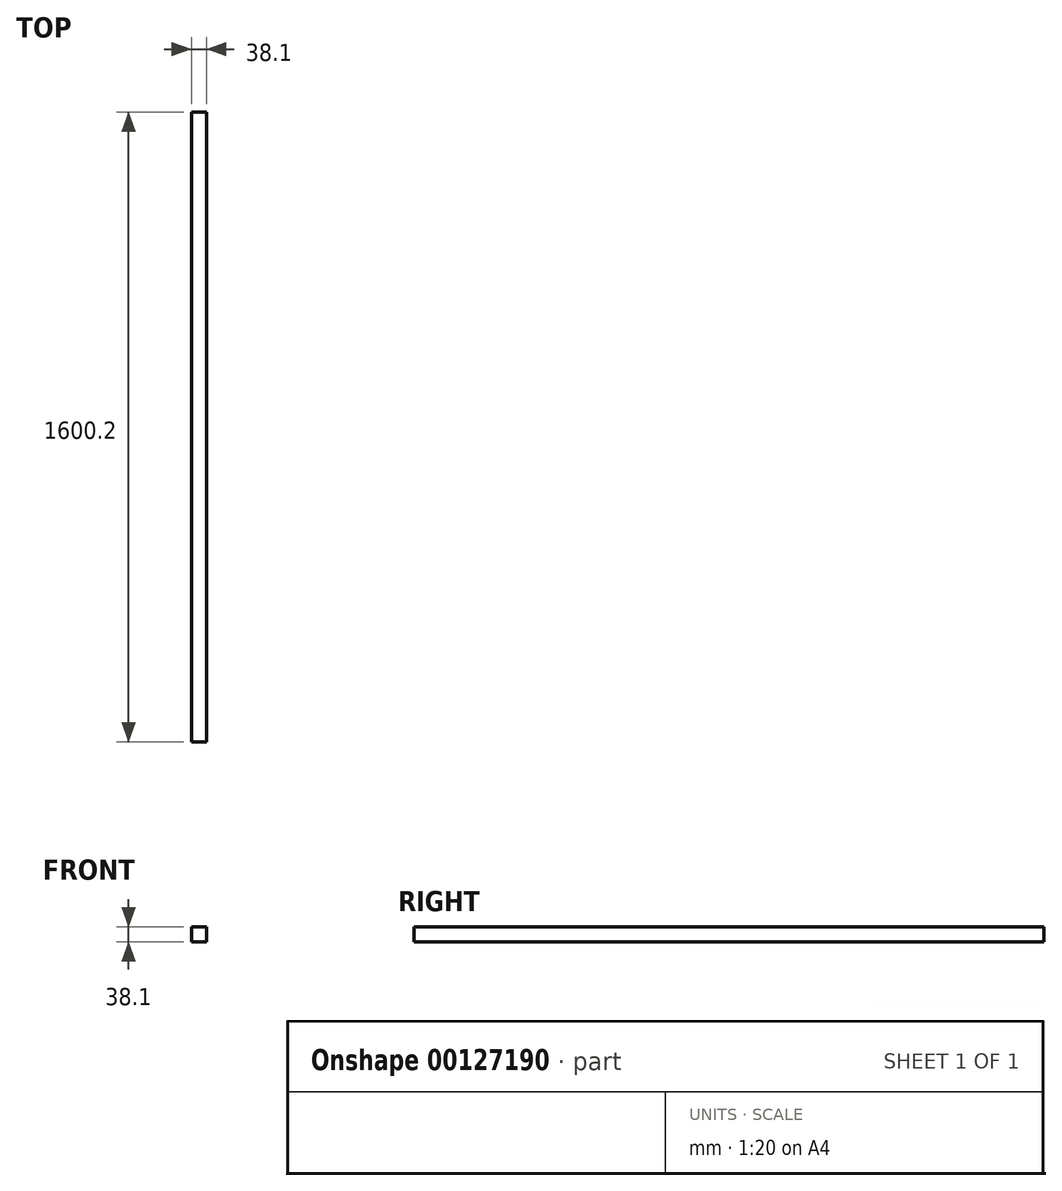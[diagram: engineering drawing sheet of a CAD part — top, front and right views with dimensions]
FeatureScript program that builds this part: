
annotation { "Feature Type Name" : "Feature", "Feature Type Description" : "" }
export const myFeature = defineFeature(function(context is Context, id is Id, definition is map)
    precondition{}
    {
        {
            var Q0;
            Q0=qCreatedBy(makeId("Front.planeOp"),FACE);
            var sketch = newSketch(context, id + "F0", { "sketchPlane" : qUnion([Q0])});
            skLineSegment(sketch, "E0.bottom", {"start": v(19.05, -19.05) * mm, "end": v(-19.05, -19.05) * mm});
            skLineSegment(sketch, "E0.top", {"start": v(19.05, 19.05) * mm, "end": v(-19.05, 19.05) * mm});
            skLineSegment(sketch, "E0.left", {"start": v(19.05, -19.05) * mm, "end": v(19.05, 19.05) * mm});
            skLineSegment(sketch, "E0.right", {"start": v(-19.05, -19.05) * mm, "end": v(-19.05, 19.05) * mm});
            skPoint(sketch, "E0.middle", {"position": v(0, 0) * mm});
            skSolve(sketch);
        }
        {
            var Q0;
            Q0=qSketchRegion(id+"F0",true);
            extrude(context, id + "F1", {"entities" : qUnion([Q0]), "depth" : 1600.2 * mm, "offsetDistance" : 25.4 * mm});
        }
    });
